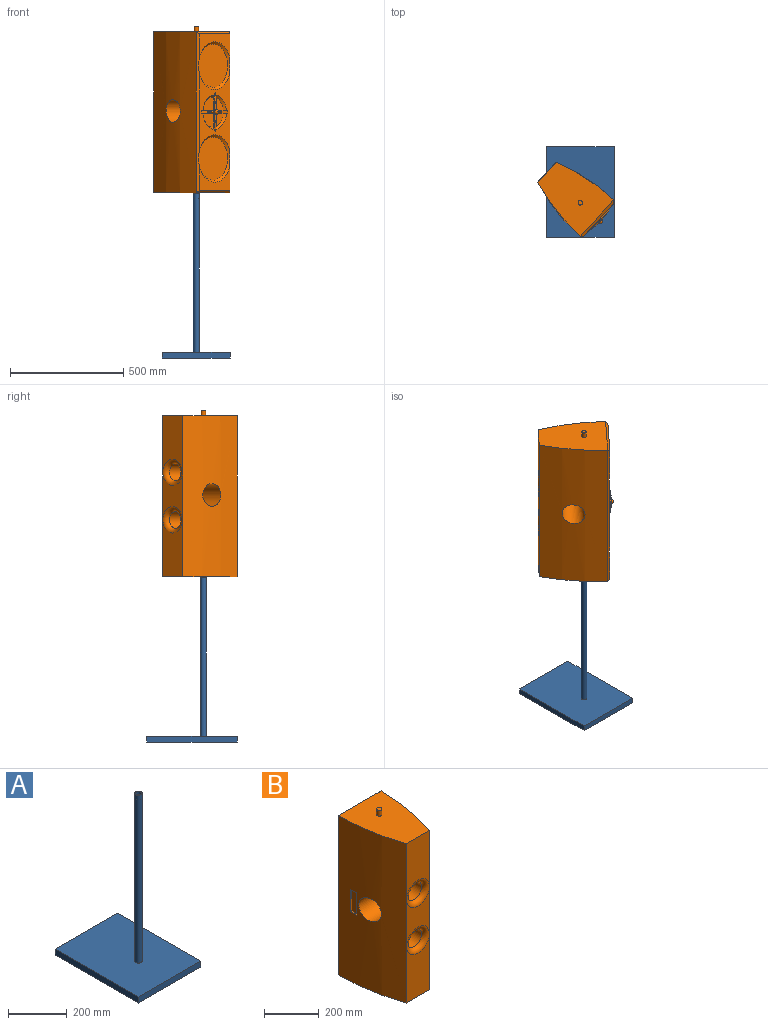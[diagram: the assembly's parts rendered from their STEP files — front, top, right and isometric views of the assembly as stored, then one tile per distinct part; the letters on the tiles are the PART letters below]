
ASSEMBLY  parts=2 mates=1
PART A: 10 faces, bbox 300x400x725 mm
  f0: plane 400x25mm, normal (-1,0,0), area 10000mm2, adj f1,f3,f4,f5
  f1: plane 300x25mm, normal (0,-1,0), area 7500mm2, adj f0,f2,f4,f5
  f2: plane 400x25mm, normal (1,0,0), area 10000mm2, adj f1,f3,f4,f5
  f3: plane 300x25mm, normal (0,1,0), area 7500mm2, adj f0,f2,f4,f5
  f4: plane 400x300mm, normal (0,0,1), area 119509.1mm2, adj f0,f1,f2,f3,f6
  f5: plane 400x300mm, normal (0,0,-1), area 120000mm2, adj f0,f1,f2,f3
  f6: cylinder r=12.5mm len=700mm, axis (0,0,-1), area 54977.9mm2, adj f4,f7
  f7: plane 25x25mm, normal (0,0,1), area 176.7mm2, adj f6,f8
  f8: cylinder r=10mm len=20mm, axis (0,0,1), area 1256.6mm2, adj f7,f9
  f9: plane 20x20mm, normal (0,0,1), area 314.2mm2, adj f8
PART B: 61 faces, bbox 220.1x330.1x760.1 mm
  f0: cylinder r=925mm len=710mm, axis (0,0,1), area 208956.8mm2, adj f3,f4,f5,f15,f55
  f1: cylinder r=925mm len=710mm, axis (0,0,1), area 205951mm2, adj f3,f4,f5,f14,f55,f56,f57,f58
  f2: plane 345.97x200mm, normal (0,1,0), area 28988mm2, adj f11,f14,f15,f16,f17,f28,f30,f31
  f3: plane 710x120mm, normal (0,-1,0), area 63990.4mm2, adj f0,f1,f4,f5,f22,f23
  f4: plane 300x220mm, normal (0,0,-1), area 55796.5mm2, adj f0,f1,f3,f12,f26
  f5: plane 300x220mm, normal (0,0,1), area 55796.5mm2, adj f0,f1,f3,f13,f24
  f6: plane 200x107.98mm, normal (0,1,0), area 10896.4mm2, adj f11,f12,f14,f15
  f7: plane 200x107.98mm, normal (0,1,0), area 10896.4mm2, adj f13,f14,f15,f16
  f8: plane 190x190mm, normal (0,1,0), area 28352.9mm2, adj f11
  f9: plane 133.35x133.35mm, normal (0,1,0), area 13966.1mm2, adj f17
  f10: plane 190x190mm, normal (0,1,0), area 28352.9mm2, adj f16
  f11: cone r=95mm half-angle=45deg, axis (0,1,0), area 8581mm2, adj f2,f6,f8,f14,f15
  f12: plane 220x10mm, normal (0,0.71,-0.71), area 2969.8mm2, adj f4,f6,f14,f15
  f13: plane 220x10mm, normal (0,0.71,0.71), area 2969.8mm2, adj f5,f7,f14,f15
  f14: plane 710x10.03mm, normal (-0.71,0.71,0), area 9597.7mm2, adj f1,f2,f6,f7,f11,f12,f13,f16
  f15: plane 710x10mm, normal (0.71,0.71,0), area 9597.6mm2, adj f0,f2,f6,f7,f11,f12,f13,f16
  f16: cone r=95mm half-angle=45deg, axis (0,1,0), area 8581mm2, adj f2,f7,f10,f14,f15
  f17: cone r=66.67mm half-angle=45deg, axis (0,1,0), area 6368.9mm2, adj f2,f9,f41
  f18: cylinder r=38.1mm len=230mm, axis (0,-1,0), area 55059.6mm2, adj f19,f22
  f19: plane 76.2x76.2mm, normal (0,-1,0), area 4560.4mm2, adj f18
  f20: cylinder r=38.1mm len=230mm, axis (0,-1,0), area 55059.6mm2, adj f21,f23
  f21: plane 76.2x76.2mm, normal (0,-1,0), area 4560.4mm2, adj f20
  f22: torus R=58.1mm, axis (0,-1,0), area 8955.2mm2, adj f3,f18
  f23: torus R=58.1mm, axis (0,-1,0), area 8955.2mm2, adj f3,f20
  f24: cylinder r=10mm len=25mm, axis (0,0,-1), area 1570.8mm2, adj f5,f25
  f25: plane 20x20mm, normal (0,0,1), area 314.2mm2, adj f24
  f26: cylinder r=10mm len=25mm, axis (0,0,1), area 1570.8mm2, adj f4,f27
  f27: plane 20x20mm, normal (0,0,-1), area 314.2mm2, adj f26
  f28: plane 73.54x5mm, normal (0,0,1), area 296.8mm2, adj f2,f29,f41,f45,f52
  f29: cylinder r=12.5mm len=12.5mm, axis (0,-1,0), area 119.2mm2, adj f28,f30,f40,f41,f50,f52
  f30: plane 73.54x5mm, normal (-1,0,0), area 296.8mm2, adj f2,f29,f41,f42,f50
  f31: plane 73.54x5mm, normal (1,0,0), area 296.8mm2, adj f2,f32,f41,f42,f51
  f32: cylinder r=12.5mm len=12.5mm, axis (0,-1,0), area 119.2mm2, adj f31,f33,f40,f41,f48,f51
  f33: plane 73.54x5mm, normal (0,0,1), area 296.8mm2, adj f2,f32,f41,f43,f48
  f34: plane 73.54x5mm, normal (0,0,-1), area 296.8mm2, adj f2,f35,f41,f43,f49
  f35: cylinder r=12.5mm len=12.5mm, axis (0,-1,0), area 119.2mm2, adj f34,f36,f40,f41,f46,f49
  f36: plane 73.54x5mm, normal (1,0,0), area 296.8mm2, adj f2,f35,f41,f44,f46
  f37: plane 73.54x5mm, normal (-1,0,0), area 296.8mm2, adj f2,f38,f41,f44,f47
  f38: cylinder r=12.5mm len=12.5mm, axis (0,-1,0), area 119.2mm2, adj f37,f39,f40,f41,f47,f53
  f39: plane 73.54x5mm, normal (0,0,-1), area 296.8mm2, adj f2,f38,f41,f45,f53
  f40: plane 25x25mm, normal (0,1,0), area 176.7mm2, adj f29,f32,f35,f38,f54
  f41: plane 153.35x153.35mm, normal (0,-1,0), area 3069.3mm2, adj f17,f28,f29,f30,f31,f32,f33,f34
  f42: plane 56.71x10mm, normal (0,0.98,0.17), area 431.9mm2, adj f2,f30,f31,f50,f51
  f43: plane 56.71x10mm, normal (0.17,0.98,0), area 431.9mm2, adj f2,f33,f34,f48,f49
  f44: plane 56.71x10mm, normal (0,0.98,-0.17), area 431.9mm2, adj f2,f36,f37,f46,f47
  f45: plane 56.71x10mm, normal (-0.17,0.98,0), area 431.9mm2, adj f2,f28,f39,f52,f53
  f46: plane 45.3x5.11mm, normal (0.71,0.71,0), area 214.3mm2, adj f35,f36,f44,f47
  f47: plane 45.3x5.11mm, normal (-0.71,0.71,0), area 214.3mm2, adj f37,f38,f44,f46
  f48: plane 45.3x5.11mm, normal (0,0.71,0.71), area 214.3mm2, adj f32,f33,f43,f49
  f49: plane 45.3x5.11mm, normal (0,0.71,-0.71), area 214.3mm2, adj f34,f35,f43,f48
  f50: plane 45.3x5.11mm, normal (-0.71,0.71,0), area 214.3mm2, adj f29,f30,f42,f51
  f51: plane 45.3x5.11mm, normal (0.71,0.71,0), area 214.3mm2, adj f31,f32,f42,f50
  f52: plane 45.3x5.11mm, normal (0,0.71,0.71), area 214.3mm2, adj f28,f29,f45,f53
  f53: plane 45.3x5.11mm, normal (0,0.71,-0.71), area 214.3mm2, adj f38,f39,f45,f52
  f54: sphere r=10mm, area 628.3mm2, adj f40
  f55: cylinder r=50mm len=209.16mm, axis (-1,0,0), area 60982.2mm2, adj f0,f1
  f56: plane 30x8.05mm, normal (0,0,1), area 207.4mm2, adj f1,f57,f59,f60
  f57: plane 100x8.05mm, normal (0,-1,0), area 805.2mm2, adj f1,f56,f58,f60
  f58: plane 30x8.05mm, normal (0,0,-1), area 207.4mm2, adj f1,f57,f59,f60
  f59: plane 100x5.61mm, normal (0,1,0), area 561.1mm2, adj f1,f56,f58,f60
  f60: plane 100x30mm, normal (-1,0,0), area 3000mm2, adj f56,f57,f58,f59
PLACE A t=(-348.46,163.77,-46.03)mm fixed
PLACE B rot(axis=(0,0,-1),132.6deg) t=(-50.39,-72.96,1393.97)mm
MATE revolute B.f24 <-> A.f6  axis (0,0,-1) through (-198.46,-86.23,658.97)mm
